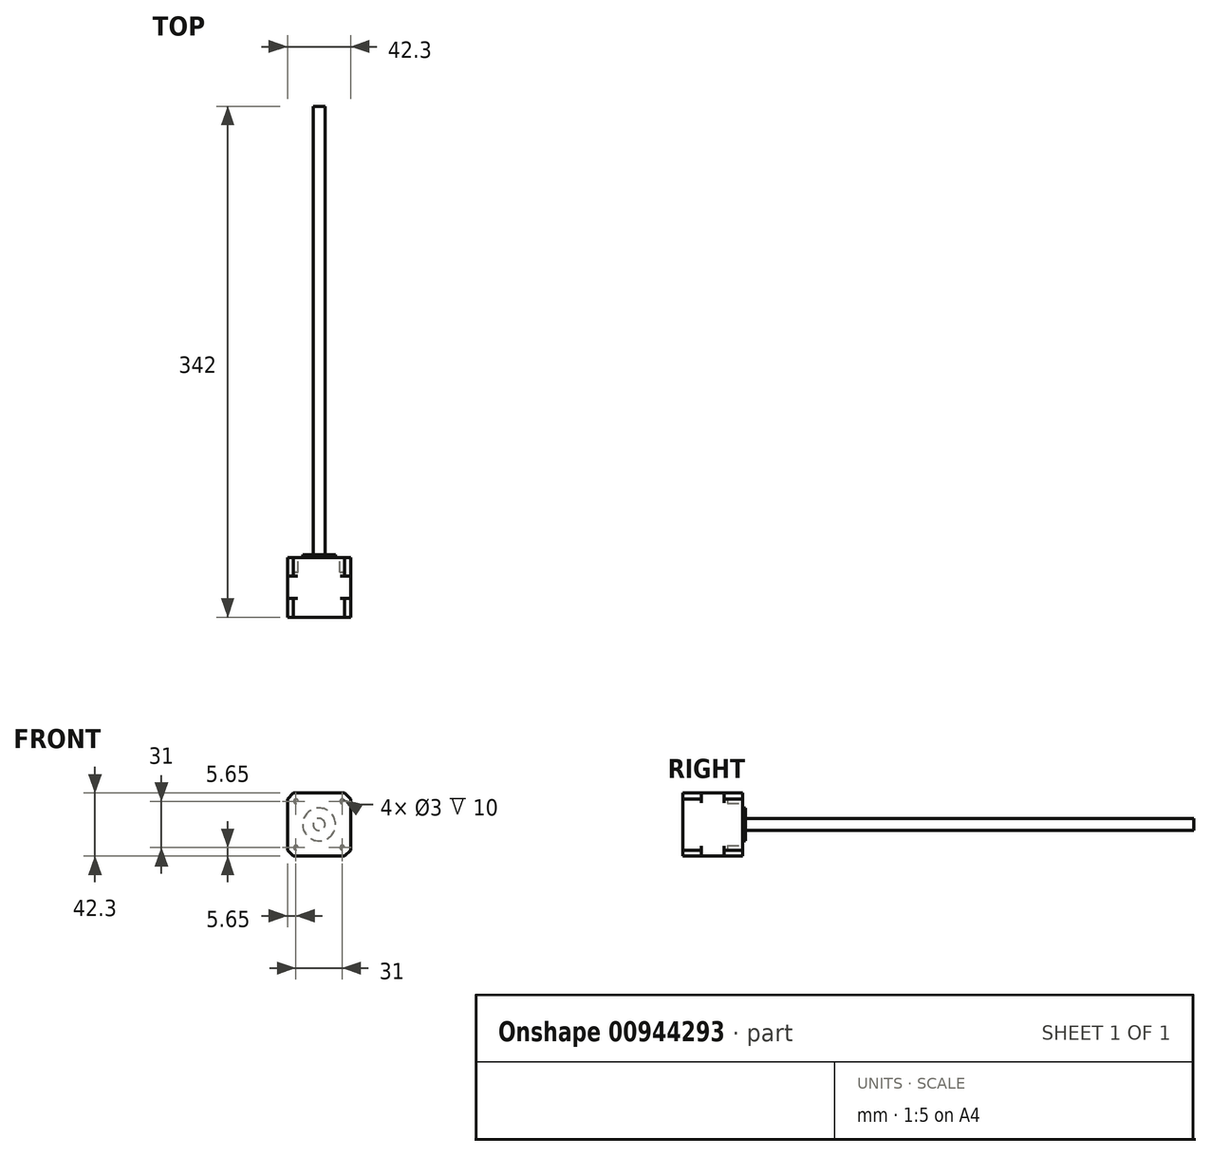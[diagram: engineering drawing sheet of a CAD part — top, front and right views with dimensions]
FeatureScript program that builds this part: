
annotation { "Feature Type Name" : "Feature", "Feature Type Description" : "" }
export const myFeature = defineFeature(function(context is Context, id is Id, definition is map)
    precondition{}
    {
        {
            var Q0;
            Q0=qCreatedBy(makeId("Front.planeOp"),FACE);
            var sketch = newSketch(context, id + "F0", { "sketchPlane" : qUnion([Q0])});
            skLineSegment(sketch, "E0.bottom", {"start": v(21.15, 21.15) * mm, "end": v(-21.15, 21.15) * mm});
            skLineSegment(sketch, "E0.top", {"start": v(21.15, -21.15) * mm, "end": v(-21.15, -21.15) * mm});
            skLineSegment(sketch, "E0.left", {"start": v(21.15, 21.15) * mm, "end": v(21.15, -21.15) * mm});
            skLineSegment(sketch, "E0.right", {"start": v(-21.15, 21.15) * mm, "end": v(-21.15, -21.15) * mm});
            skPoint(sketch, "E0.middle", {"position": v(0, 0) * mm});
            skPoint(sketch, "E1.visualSharp", {"position": v(-21.15, 21.15) * mm});
            skPoint(sketch, "E2.orphan", {"position": v(21.15, 21.15) * mm});
            skPoint(sketch, "E3.orphan", {"position": v(21.15, -21.15) * mm});
            skPoint(sketch, "E4.orphan", {"position": v(-21.15, -21.15) * mm});
            skSolve(sketch);
        }
        {
            var Q0;
            Q0=makeQuery(id+"F0.imprint","IMPRINT",FACE,{"disambiguationData":[TD([[makeQuery(id+"F0.imprint","IMPRINT",EDGE,{"derivedFrom":sQuery(id+"F0.wireOp",EDGE,"E0.bottom")}),1.0]])]});
            extrude(context, id + "F1", {"entities" : qUnion([Q0]), "depth" : 40 * mm, "offsetDistance" : 25 * mm});
        }
        {
            var Q0;
            Q0=makeQuery(id+"F1.opExtrude","CAP_FACE",FACE,{"disambiguationData":[OSD([sQuery(id+"F0.wireOp",EDGE,"E0.bottom"),sQuery(id+"F0.wireOp",EDGE,"E0.top"),sQuery(id+"F0.wireOp",EDGE,"E0.left"),sQuery(id+"F0.wireOp",EDGE,"E0.right"),sQuery(id+"F0.wireOp",EDGE,"Xe1pNUPd-5NHr-yC4v-04eJ-njersvvzofgt"),sQuery(id+"F0.wireOp",EDGE,"3830abb2-49cd-4b53-8be5-f5c9399e15470.MirrorC"),sQuery(id+"F0.wireOp",EDGE,"f7871d61-49dc-4b65-b8a3-a071d65dc2940.MirrorC"),sQuery(id+"F0.wireOp",EDGE,"5f0c8ad3-0e0d-44d6-be3f-279486d6b9530.MirrorC"),sQuery(id+"F0.wireOp",EDGE,"E1.filletArc"),sQuery(id+"F0.wireOp",EDGE,"bb470a36-2f72-4c16-97b8-b32c393a97940.MirrorCS"),sQuery(id+"F0.wireOp",EDGE,"2c940c82-93c7-4399-86c2-3b0c11c1d09e0.MirrorCS"),sQuery(id+"F0.wireOp",EDGE,"18518c19-3f0e-4304-99dd-ba4c207d6b000.MirrorCS")])],"isStart":true});
            var sketch = newSketch(context, id + "F2", { "sketchPlane" : qUnion([Q0])});
            skCircle(sketch, "E5", {"center": v(0, 0) * mm, "radius": 11 * mm});
            skSolve(sketch);
        }
        {
            var Q0;
            Q0=makeQuery(id+"F2.imprint","IMPRINT",FACE,{"disambiguationData":[TD([[makeQuery(id+"F2.imprint","IMPRINT",EDGE,{"derivedFrom":sQuery(id+"F2.wireOp",EDGE,"E5")}),1.0]])]});
            extrude(context, id + "F3", {"entities" : qUnion([Q0]), "operationType" : NewBodyOperationType.ADD, "depth" : 2 * mm, "offsetDistance" : 25 * mm});
        }
        {
            var Q0;
            Q0=makeQuery(id+"F3.opExtrude","CAP_FACE",FACE,{"disambiguationData":[OSD([sQuery(id+"F2.wireOp",EDGE,"E5")])],"isStart":false});
            var sketch = newSketch(context, id + "F4", { "sketchPlane" : qUnion([Q0])});
            skCircle(sketch, "E6", {"center": v(0, 0) * mm, "radius": 4 * mm});
            skSolve(sketch);
        }
        {
            var Q0;
            Q0=makeQuery(id+"F4.imprint","IMPRINT",FACE,{"disambiguationData":[TD([[makeQuery(id+"F4.imprint","IMPRINT",EDGE,{"derivedFrom":sQuery(id+"F4.wireOp",EDGE,"E6")}),1.0]])]});
            extrude(context, id + "F5", {"entities" : qUnion([Q0]), "operationType" : NewBodyOperationType.ADD, "depth" : 300 * mm, "offsetDistance" : 25 * mm});
        }
        {
            var Q0;
            Q0=makeQuery(id+"F1.opExtrude","SWEPT_EDGE",EDGE,{"disambiguationData":[OSD([sQuery(id+"F0.wireOp",EDGE,"E0.bottom"),sQuery(id+"F0.wireOp",EDGE,"E0.right")])]});
            var Q1;
            Q1=makeQuery(id+"F1.opExtrude","SWEPT_EDGE",EDGE,{"disambiguationData":[OSD([sQuery(id+"F0.wireOp",EDGE,"E0.top"),sQuery(id+"F0.wireOp",EDGE,"E0.right")])]});
            var Q2;
            Q2=makeQuery(id+"F1.opExtrude","SWEPT_EDGE",EDGE,{"disambiguationData":[OSD([sQuery(id+"F0.wireOp",EDGE,"E0.top"),sQuery(id+"F0.wireOp",EDGE,"E0.left")])]});
            var Q3;
            Q3=makeQuery(id+"F1.opExtrude","SWEPT_EDGE",EDGE,{"disambiguationData":[OSD([sQuery(id+"F0.wireOp",EDGE,"E0.bottom"),sQuery(id+"F0.wireOp",EDGE,"E0.left")])]});
            chamfer(context, id + "F6", {"entities" : qUnion([Q0, Q1, Q2, Q3]), "width" : 4 * mm, "tangentPropagation" : true});
        }
        {
            var Q0;
            Q0=qCreatedBy(makeId("Front.planeOp"),FACE);
            cPlane(context, id + "F7", {"entities" : qUnion([Q0]), "cplaneType" : CPlaneType.OFFSET, "offset" : 20 * mm, "width" : 150 * mm, "height" : 150 * mm});
        }
        {
            var Q0;
            Q0=qCreatedBy(id+"F7.planeOp",FACE);
            var sketch = newSketch(context, id + "F8", { "sketchPlane" : qUnion([Q0])});
            skLineSegment(sketch, "E7", {"start": v(21.15, 0) * mm, "end": v(21.15, 14.32) * mm});
            skLineSegment(sketch, "E8", {"start": v(0, 21.15) * mm, "end": v(14.32, 21.15) * mm});
            skArc(sketch, "E9", {"start": v(21.15, 14.32) * mm, "mid": v(19.15, 19.15) * mm, "end": v(14.32, 21.15) * mm});
            skLineSegment(sketch, "E10", {"start": v(21.15, 14.32) * mm, "end": v(21.15, 21.15) * mm});
            skLineSegment(sketch, "E11", {"start": v(21.15, 21.15) * mm, "end": v(14.32, 21.15) * mm});
            skArc(sketch, "E12.MirrorCS", {"start": v(-21.15, 14.32) * mm, "mid": v(-19.15, 19.15) * mm, "end": v(-14.32, 21.15) * mm});
            skLineSegment(sketch, "E13.MirrorCS", {"start": v(-21.15, 21.15) * mm, "end": v(-14.32, 21.15) * mm});
            skLineSegment(sketch, "E14.MirrorCS", {"start": v(-21.15, 14.32) * mm, "end": v(-21.15, 21.15) * mm});
            skArc(sketch, "E15.MirrorCS", {"start": v(21.15, -14.32) * mm, "mid": v(19.15, -19.15) * mm, "end": v(14.32, -21.15) * mm});
            skLineSegment(sketch, "E16.MirrorCS", {"start": v(21.15, -14.32) * mm, "end": v(21.15, -21.15) * mm});
            skLineSegment(sketch, "E17.MirrorCS", {"start": v(21.15, -21.15) * mm, "end": v(14.32, -21.15) * mm});
            skArc(sketch, "E18.MirrorCS", {"start": v(-21.15, -14.32) * mm, "mid": v(-19.15, -19.15) * mm, "end": v(-14.32, -21.15) * mm});
            skLineSegment(sketch, "E19.MirrorCS", {"start": v(-21.15, -21.15) * mm, "end": v(-14.32, -21.15) * mm});
            skLineSegment(sketch, "E20.MirrorCS", {"start": v(-21.15, -14.32) * mm, "end": v(-21.15, -21.15) * mm});
            skSolve(sketch);
        }
        {
            var Q0;
            Q0=qSketchRegion(id+"F8",true);
            extrude(context, id + "F9", {"entities" : qUnion([Q0]), "operationType" : NewBodyOperationType.REMOVE, "depth" : 15 * mm, "offsetDistance" : 25 * mm, "symmetric" : true});
        }
        {
            var Q0;
            Q0=makeQuery(id+"F1.opExtrude","CAP_FACE",FACE,{"disambiguationData":[OSD([sQuery(id+"F0.wireOp",EDGE,"E0.bottom"),sQuery(id+"F0.wireOp",EDGE,"E0.top"),sQuery(id+"F0.wireOp",EDGE,"E0.left"),sQuery(id+"F0.wireOp",EDGE,"E0.right")])],"isStart":true});
            var sketch = newSketch(context, id + "F10", { "sketchPlane" : qUnion([Q0])});
            skCircle(sketch, "E21", {"center": v(-15.5, 15.5) * mm, "radius": 1.5 * mm});
            skCircle(sketch, "E22.MirrorC", {"center": v(15.5, 15.5) * mm, "radius": 1.5 * mm});
            skCircle(sketch, "E23.MirrorC", {"center": v(-15.5, -15.5) * mm, "radius": 1.5 * mm});
            skCircle(sketch, "E24.MirrorC", {"center": v(15.5, -15.5) * mm, "radius": 1.5 * mm});
            skSolve(sketch);
        }
        {
            var Q0;
            Q0=qSketchRegion(id+"F10",true);
            extrude(context, id + "F11", {"entities" : qUnion([Q0]), "operationType" : NewBodyOperationType.REMOVE, "oppositeDirection" : true, "depth" : 10 * mm, "offsetDistance" : 25 * mm});
        }
    });
